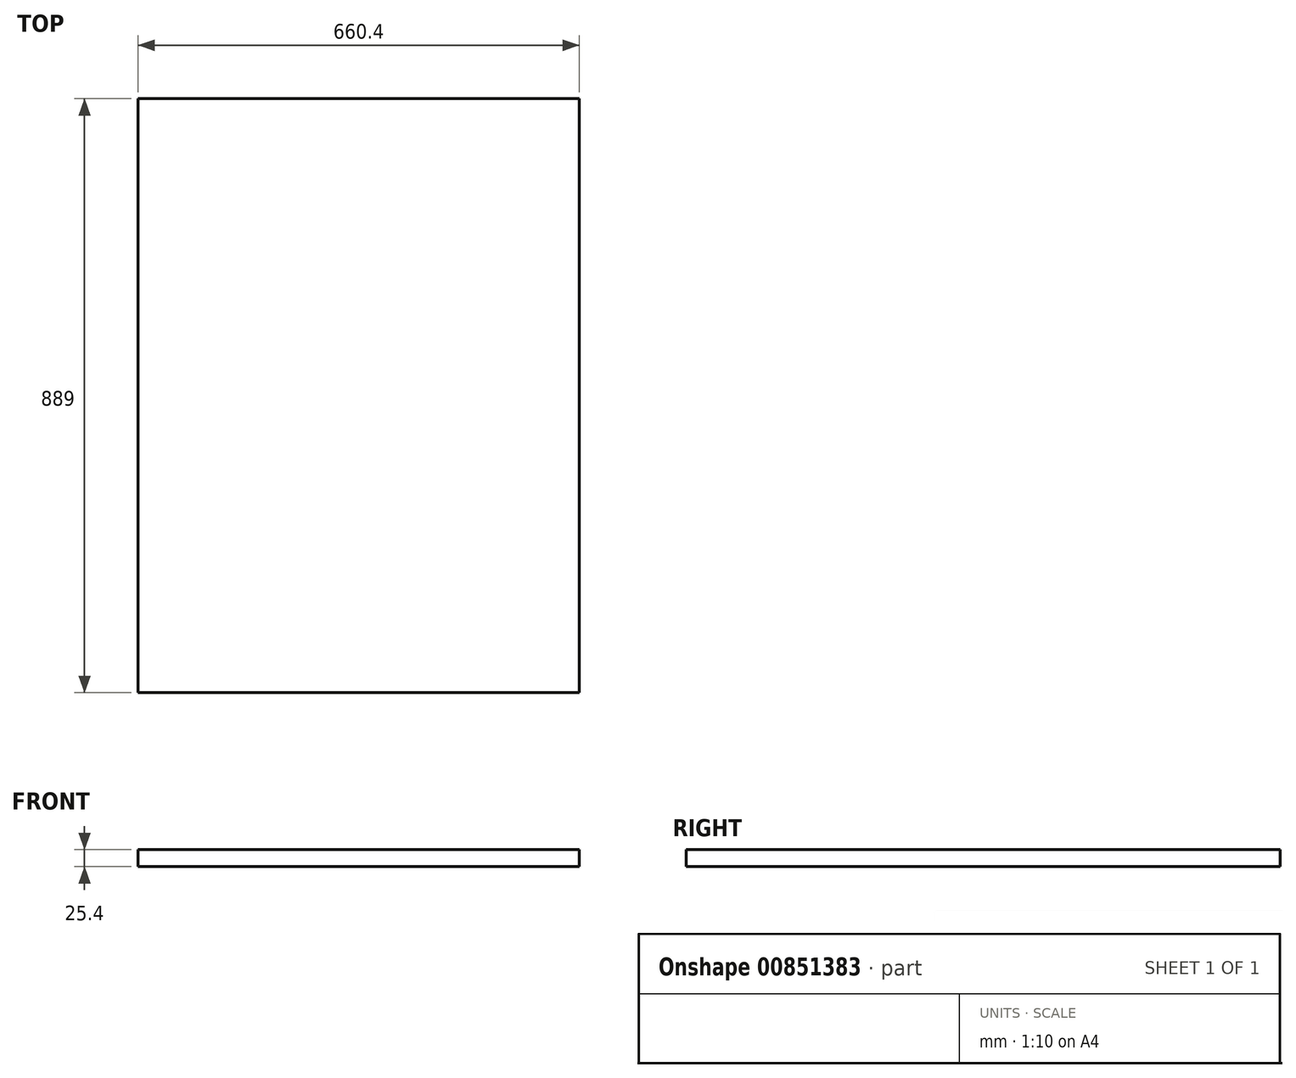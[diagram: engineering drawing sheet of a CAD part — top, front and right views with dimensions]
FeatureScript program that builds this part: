
annotation { "Feature Type Name" : "Feature", "Feature Type Description" : "" }
export const myFeature = defineFeature(function(context is Context, id is Id, definition is map)
    precondition{}
    {
        {
            var Q0;
            Q0=qCreatedBy(makeId("Top.planeOp"),FACE);
            var sketch = newSketch(context, id + "F0", { "sketchPlane" : qUnion([Q0])});
            skLineSegment(sketch, "E0.bottom", {"start": v(-332.95, 716.44) * mm, "end": v(327.45, 716.44) * mm});
            skLineSegment(sketch, "E0.top", {"start": v(-332.95, -172.56) * mm, "end": v(327.45, -172.56) * mm});
            skLineSegment(sketch, "E0.left", {"start": v(-332.95, 716.44) * mm, "end": v(-332.95, -172.56) * mm});
            skLineSegment(sketch, "E0.right", {"start": v(327.45, 716.44) * mm, "end": v(327.45, -172.56) * mm});
            skSolve(sketch);
        }
        {
            var Q0;
            Q0 = qSketchRegion(id + "F0", true);
            extrude(context, id + "F1", {"entities" : qUnion([Q0]), "depth" : 25.4 * mm, "offsetDistance" : 25.4 * mm});
        }
    });
